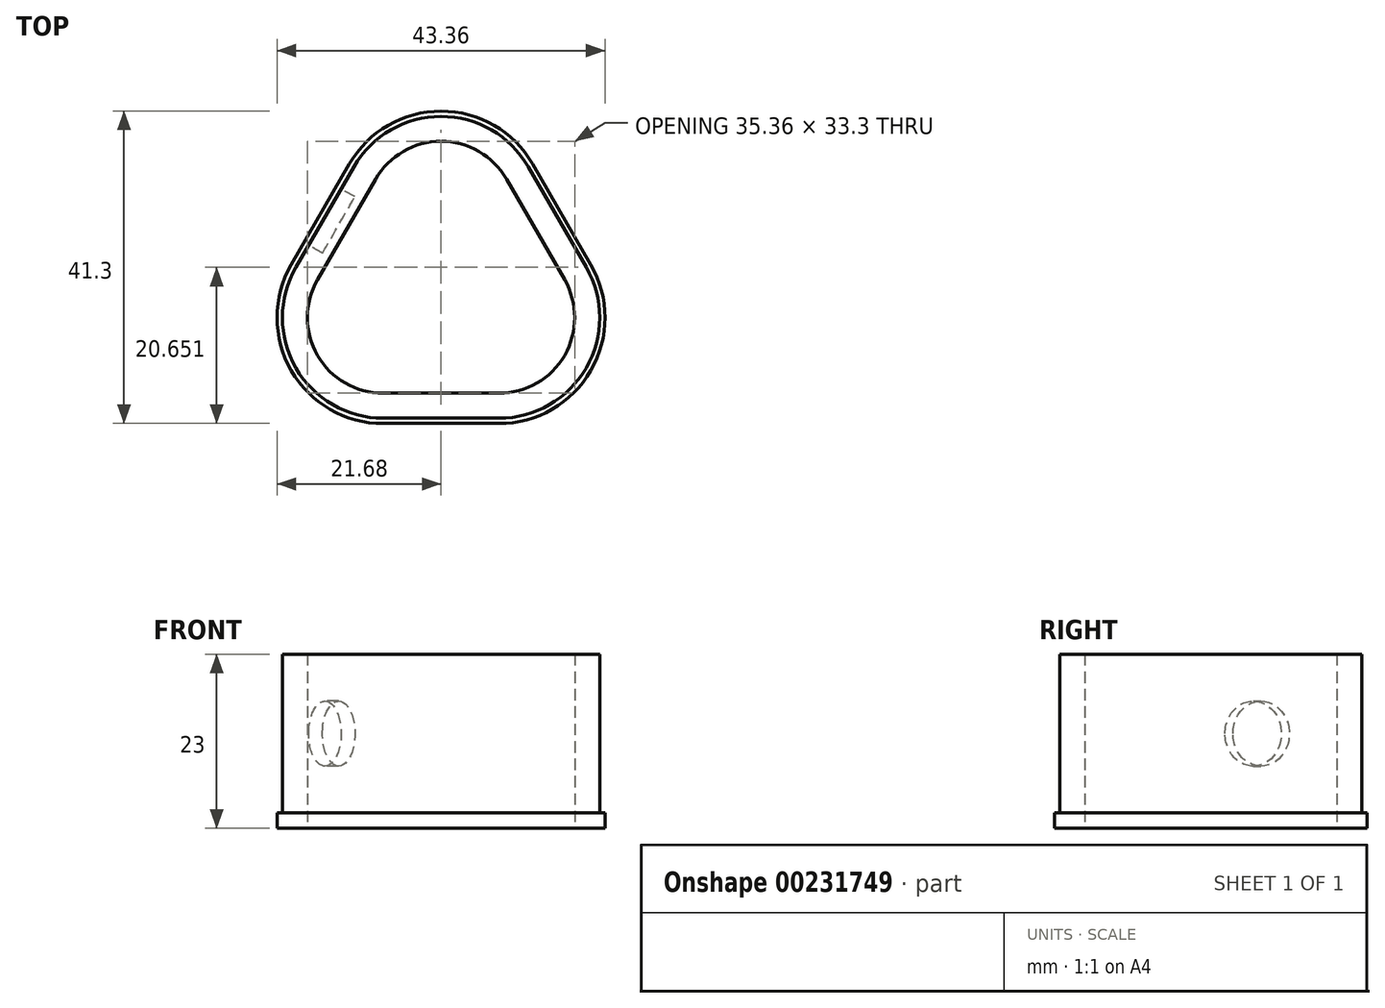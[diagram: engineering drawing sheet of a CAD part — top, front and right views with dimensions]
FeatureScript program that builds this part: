
annotation { "Feature Type Name" : "Feature", "Feature Type Description" : "" }
export const myFeature = defineFeature(function(context is Context, id is Id, definition is map)
    precondition{}
    {
        {
            var Q0;
            Q0=qCreatedBy(makeId("Top.planeOp"),FACE);
            var sketch = newSketch(context, id + "F0", { "sketchPlane" : qUnion([Q0])});
            skLineSegment(sketch, "E0", {"start": v(0, 0) * mm, "end": v(7.68, 0) * mm});
            skLineSegment(sketch, "E1", {"start": v(16.34, 15) * mm, "end": v(8.66, 28.3) * mm});
            skLineSegment(sketch, "E2", {"start": v(-8.66, 28.3) * mm, "end": v(-16.34, 15) * mm});
            skLineSegment(sketch, "E3", {"start": v(-7.68, 0) * mm, "end": v(0, 0) * mm});
            skLineSegment(sketch, "E4", {"start": v(0, 0) * mm, "end": v(0, 43.3) * mm, "construction": true});
            skLineSegment(sketch, "E5", {"start": v(-12.5, 21.65) * mm, "end": v(25, 0) * mm, "construction": true});
            skLineSegment(sketch, "E6", {"start": v(12.5, 21.65) * mm, "end": v(-25, 0) * mm, "construction": true});
            skCircle(sketch, "E7", {"center": v(0, 14.43) * mm, "radius": 12.5 * mm});
            skPoint(sketch, "E8.visualSharp", {"position": v(0, 43.3) * mm});
            skArc(sketch, "E8.filletArc", {"start": v(8.66, 28.3) * mm, "mid": v(0, 33.3) * mm, "end": v(-8.66, 28.3) * mm});
            skPoint(sketch, "E9.visualSharp", {"position": v(-25, 0) * mm});
            skArc(sketch, "E9.filletArc", {"start": v(-16.34, 15) * mm, "mid": v(-16.34, 5) * mm, "end": v(-7.68, 0) * mm});
            skPoint(sketch, "E10.visualSharp", {"position": v(25, 0) * mm});
            skArc(sketch, "E10.filletArc", {"start": v(7.68, 0) * mm, "mid": v(16.34, 5) * mm, "end": v(16.34, 15) * mm});
            skLineSegment(sketch, "E11.0", {"start": v(19.8, 17) * mm, "end": v(12.12, 30.3) * mm});
            skArc(sketch, "E11.1", {"start": v(7.68, -4) * mm, "mid": v(19.8, 3) * mm, "end": v(19.8, 17) * mm});
            skLineSegment(sketch, "E11.2", {"start": v(-12.12, 30.3) * mm, "end": v(-19.8, 17) * mm});
            skArc(sketch, "E11.3", {"start": v(-19.8, 17) * mm, "mid": v(-19.8, 3) * mm, "end": v(-7.68, -4) * mm});
            skLineSegment(sketch, "E11.4", {"start": v(-7.68, -4) * mm, "end": v(0, -4) * mm});
            skArc(sketch, "E11.5", {"start": v(12.12, 30.3) * mm, "mid": v(0, 37.3) * mm, "end": v(-12.12, 30.3) * mm});
            skLineSegment(sketch, "E11.6", {"start": v(0, -4) * mm, "end": v(7.68, -4) * mm});
            skSolve(sketch);
        }
        {
            var Q0;
            Q0=makeQuery(id+"F0.imprint","IMPRINT",FACE,{"disambiguationData":[TD([[makeQuery(id+"F0.imprint","IMPRINT",EDGE,{"derivedFrom":sQuery(id+"F0.wireOp",EDGE,"E0")}),-1.0]])]});
            extrude(context, id + "F1", {"entities" : qUnion([Q0]), "depth" : 25 * mm});
        }
        {
            var Q0;
            Q0=makeQuery(id+"F1.opExtrude","SWEPT_FACE",FACE,{"disambiguationData":[OSD([sQuery(id+"F0.wireOp",EDGE,"E11.2")])]});
            var sketch = newSketch(context, id + "F2", { "sketchPlane" : qUnion([Q0])});
            skCircle(sketch, "E12", {"center": v(-12.5, 12.5) * mm, "radius": 4.3 * mm});
            skPoint(sketch, "E12.centerSnap0", {"position": v(-12.5, 25) * mm});
            skPoint(sketch, "E12.centerSnap1", {"position": v(-20.18, 12.5) * mm});
            skSolve(sketch);
        }
        {
            var Q0;
            Q0=qSketchRegion(id+"F2",true);
            extrude(context, id + "F3", {"entities" : qUnion([Q0]), "operationType" : NewBodyOperationType.REMOVE, "oppositeDirection" : true, "depth" : 2.8 * mm, "hasSecondDirection" : true, "secondDirectionOppositeDirection" : true, "secondDirectionDepth" : 0.65 * mm});
        }
        {
            var Q0;
            Q0=makeQuery(id+"F1.opExtrude","CAP_FACE",FACE,{"disambiguationData":[OSD([sQuery(id+"F0.wireOp",EDGE,"E0"),sQuery(id+"F0.wireOp",EDGE,"E1"),sQuery(id+"F0.wireOp",EDGE,"E2"),sQuery(id+"F0.wireOp",EDGE,"E3"),sQuery(id+"F0.wireOp",EDGE,"E8.filletArc"),sQuery(id+"F0.wireOp",EDGE,"E9.filletArc"),sQuery(id+"F0.wireOp",EDGE,"E10.filletArc"),sQuery(id+"F0.wireOp",EDGE,"E11.0"),sQuery(id+"F0.wireOp",EDGE,"E11.1"),sQuery(id+"F0.wireOp",EDGE,"E11.2"),sQuery(id+"F0.wireOp",EDGE,"E11.3"),sQuery(id+"F0.wireOp",EDGE,"E11.4"),sQuery(id+"F0.wireOp",EDGE,"E11.5"),sQuery(id+"F0.wireOp",EDGE,"E11.6")])],"isStart":false});
            var sketch = newSketch(context, id + "F4", { "sketchPlane" : qUnion([Q0])});
            skLineSegment(sketch, "E13", {"start": v(-12.5, 21.65) * mm, "end": v(16.34, 5) * mm});
            skLineSegment(sketch, "E14", {"start": v(16.34, 5) * mm, "end": v(0, 0) * mm});
            skLineSegment(sketch, "E15", {"start": v(0, 0) * mm, "end": v(0, 33.3) * mm});
            skCircle(sketch, "E16", {"center": v(0, 14.43) * mm, "radius": 3.2 * mm});
            skSolve(sketch);
        }
        {
            var Q0;
            Q0=makeQuery(id+"F1.opExtrude","CAP_FACE",FACE,{"disambiguationData":[OSD([sQuery(id+"F0.wireOp",EDGE,"E0"),sQuery(id+"F0.wireOp",EDGE,"E1"),sQuery(id+"F0.wireOp",EDGE,"E2"),sQuery(id+"F0.wireOp",EDGE,"E3"),sQuery(id+"F0.wireOp",EDGE,"E8.filletArc"),sQuery(id+"F0.wireOp",EDGE,"E9.filletArc"),sQuery(id+"F0.wireOp",EDGE,"E10.filletArc"),sQuery(id+"F0.wireOp",EDGE,"E11.0"),sQuery(id+"F0.wireOp",EDGE,"E11.1"),sQuery(id+"F0.wireOp",EDGE,"E11.2"),sQuery(id+"F0.wireOp",EDGE,"E11.3"),sQuery(id+"F0.wireOp",EDGE,"E11.4"),sQuery(id+"F0.wireOp",EDGE,"E11.5"),sQuery(id+"F0.wireOp",EDGE,"E11.6")])],"isStart":false});
            var sketch = newSketch(context, id + "F5", { "sketchPlane" : qUnion([Q0])});
            skSolve(sketch);
        }
        {
            var Q0;
            Q0=makeQuery(id+"F5.imprint","IMPRINT",FACE,{"disambiguationData":[TD([[makeQuery(id+"F5.imprint","IMPRINT",EDGE,{"derivedFrom":makeQuery(id+"F1.opExtrude","CAP_EDGE",EDGE,{"disambiguationData":[OSD([sQuery(id+"F0.wireOp",EDGE,"E1")])],"isStart":false})}),-1.0]])]});
            var sketch = newSketch(context, id + "F6", { "sketchPlane" : qUnion([Q0])});
            skCircle(sketch, "E17", {"center": v(0, 15.2) * mm, "radius": 33.7 * mm});
            skSolve(sketch);
        }
        {
            var Q0;
            Q0 = qSketchRegion(id + "F6", true);
            extrude(context, id + "F7", {"entities" : qUnion([Q0]), "operationType" : NewBodyOperationType.REMOVE, "oppositeDirection" : true, "depth" : 2 * mm});
        }
        {
            var Q0;
            Q0=makeQuery(id+"F7.boolean.opBoolean","COPY",FACE,{"derivedFrom":makeQuery(id+"F7.opExtrude","CAP_FACE",FACE,{"disambiguationData":[OSD([sQuery(id+"F6.wireOp",EDGE,"E17")])],"isStart":false})});
            var sketch = newSketch(context, id + "F8", { "sketchPlane" : qUnion([Q0])});
            skArc(sketch, "E18.0", {"start": v(11.52, 29.95) * mm, "mid": v(0, 36.6) * mm, "end": v(-11.52, 29.95) * mm});
            skArc(sketch, "E18.1", {"start": v(-19.2, 16.65) * mm, "mid": v(-19.2, 3.35) * mm, "end": v(-7.68, -3.3) * mm});
            skLineSegment(sketch, "E18.2", {"start": v(-7.68, -3.3) * mm, "end": v(7.68, -3.3) * mm});
            skLineSegment(sketch, "E18.3", {"start": v(-11.52, 29.95) * mm, "end": v(-19.2, 16.65) * mm});
            skArc(sketch, "E18.4", {"start": v(7.68, -3.3) * mm, "mid": v(19.2, 3.35) * mm, "end": v(19.2, 16.65) * mm});
            skLineSegment(sketch, "E18.5", {"start": v(19.2, 16.65) * mm, "end": v(11.52, 29.95) * mm});
            skSolve(sketch);
        }
        {
            var Q0;
            Q0=makeQuery(id+"F8.imprint","IMPRINT",FACE,{"disambiguationData":[TD([[makeQuery(id+"F8.imprint","IMPRINT",EDGE,{"derivedFrom":sQuery(id+"F8.wireOp",EDGE,"E18.0")}),-1.0]])]});
            extrude(context, id + "F9", {"entities" : qUnion([Q0]), "operationType" : NewBodyOperationType.REMOVE, "oppositeDirection" : true, "depth" : 21 * mm});
        }
    });
